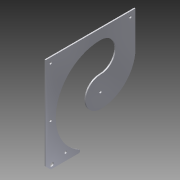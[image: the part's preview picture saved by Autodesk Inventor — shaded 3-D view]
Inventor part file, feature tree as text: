
AUTODESK INVENTOR PART (.ipt)
format: ipt  version: 2015 (Build 190159000, 159)  size: 207,872 bytes
history: native  units: in
note: dims shown in document units (in); Inventor stores cm internally (conversion verified against a paired STEP export)
features: sketch x6, projected_geometry x5, extrude x4, hole x2, fillet x1
ambient origin geometry x8: Origin, YZ Plane, XZ Plane, XY Plane, X Axis, Y Axis, Z Axis, Center Point
bodies: Solid1 (feature_tree)
feature tree (18):
  extrude  "Extrusion1"  Depth=2.5in
  extrude  "Extrusion2"  Depth=3.25in
  hole  "Hole1"  [1 undecoded]
  sketch  "Sketch4"  dims[d6=0.0in d7=9.0in]
  extrude  "Extrusion4"  Depth=9.0in
  hole  "Hole3"  [1 undecoded]
  fillet  "Fillet1"  Radius=7.0in
  extrude  "Extrusion5"  Depth=0.125in
  sketch  "Sketch1"  dims[d0=4.0in d1=2.5in]
  sketch  "Sketch2"  dims[d2=2.5in d3=3.25in]
  projected_geometry  "Projected Loop1"
  sketch  "Sketch3"  dims[d4=3.25in d5=0.0in]
  projected_geometry  "Projected Loop2"
  projected_geometry  "Projected Loop3"
  sketch  "Sketch5"  dims[d8=3.0in d9=3.0in d10=7.0in]
  projected_geometry  "Projected Loop4"
  sketch  "Sketch6"  dims[d11=3.5in d12=5.5in d13=0.0in d14=10.0in d15=5.5in d16=0.0in d17=2.3125in d18=4.0in d22=0.125in d23=0.0in d24=3.0in d25=0.25in d26=0.5in d27=0.125in d28=0.0in d29=0.5in d30=0.5in d31=0.5in d32=0.5in d33=0.5in d34=5.5in d35=3.5in d36=3.5in d37=0.25in d38=0.75in d39=0.375in d40=0.25in d41=0.5635in d42=1.0in d43=0.8108in d55=0.25in d60=0.5in d61=0.5in d62=0.125in d63=0.0in d64=0.625in d65=0.375in d66=0.375in d67=0.75in d68=0.375in d69=0.25in d70=0.5635in d71=1.0in d72=0.8108in d73=0.125in d74=1.0in d75=0.0in]
  projected_geometry  "Projected Loop5"
note: 2 required parameter values undecoded (feature->parameter linkage not recoverable at this tier; creation-order binding heuristic only, values carry confidence <= 0.55)
